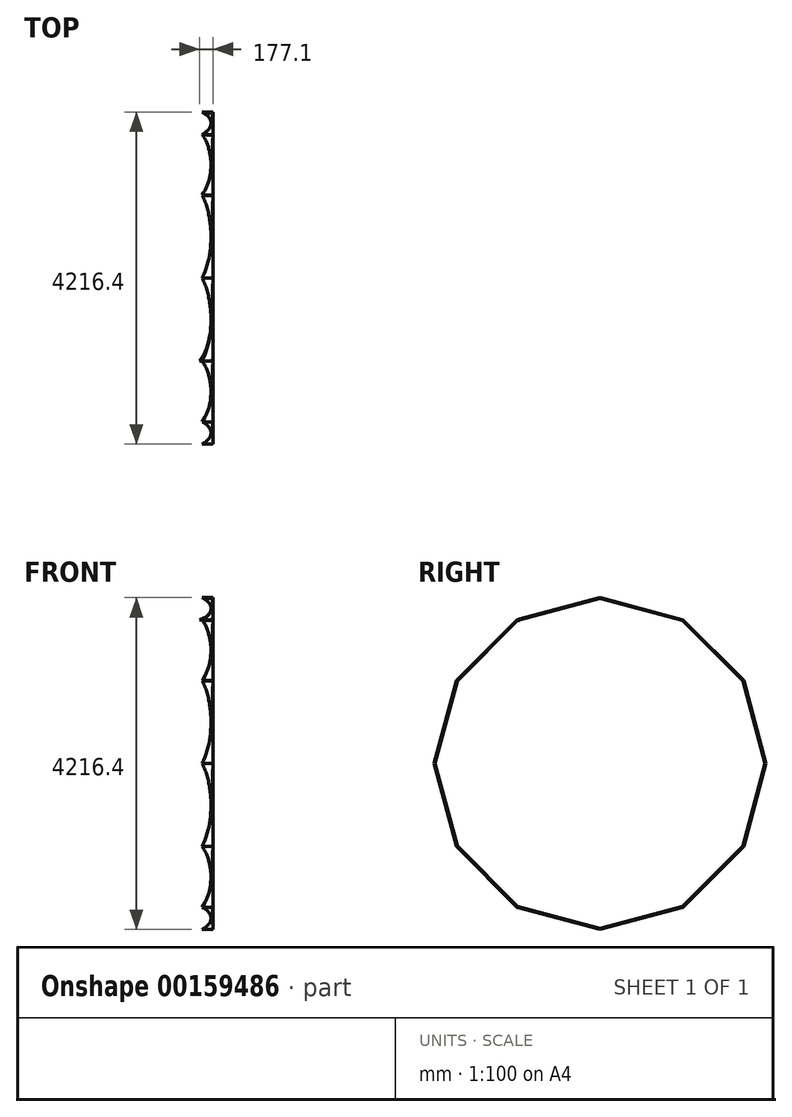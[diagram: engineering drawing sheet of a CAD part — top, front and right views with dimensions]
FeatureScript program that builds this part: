
annotation { "Feature Type Name" : "Feature", "Feature Type Description" : "" }
export const myFeature = defineFeature(function(context is Context, id is Id, definition is map)
    precondition{}
    {
        {
            var Q0;
            Q0=qCreatedBy(makeId("Top.planeOp"),FACE);
            var sketch = newSketch(context, id + "F0", { "sketchPlane" : qUnion([Q0])});
            skCircle(sketch, "E0", {"center": v(0, 0) * mm, "radius": 2159 * mm, "construction": true});
            skCircle(sketch, "E1.1.0.0", {"center": v(2159, 0) * mm, "radius": 2159 * mm, "construction": true});
            skCircle(sketch, "E1.2.0.0", {"center": v(4318, 0) * mm, "radius": 2159 * mm, "construction": true});
            skCircle(sketch, "E1.3.0.0", {"center": v(6477, 0) * mm, "radius": 2159 * mm, "construction": true});
            skLineSegment(sketch, "E1.direction1", {"start": v(0, 0) * mm, "end": v(2159, 0) * mm, "construction": true});
            skLineSegment(sketch, "E2", {"start": v(0, 0) * mm, "end": v(-6666.76, 0) * mm, "construction": true});
            skLineSegment(sketch, "E3", {"start": v(0, 0) * mm, "end": v(-3812.7, 2201.26) * mm, "construction": true});
            skLineSegment(sketch, "E4", {"start": v(0, 0) * mm, "end": v(0, 5036.56) * mm, "construction": true});
            skLineSegment(sketch, "E5", {"start": v(0, 0) * mm, "end": v(5007.78, 2891.24) * mm, "construction": true});
            skCircle(sketch, "E6.MirrorC", {"center": v(2159, 3739.5) * mm, "radius": 2159 * mm, "construction": true});
            skCircle(sketch, "E7.MirrorC", {"center": v(3238.5, 5609.25) * mm, "radius": 2159 * mm, "construction": true});
            skCircle(sketch, "E8.MirrorC", {"center": v(1079.5, 1869.75) * mm, "radius": 2159 * mm, "construction": true});
            skCircle(sketch, "E9.MirrorC", {"center": v(-3238.5, 5609.25) * mm, "radius": 2159 * mm, "construction": true});
            skCircle(sketch, "E10.MirrorC", {"center": v(-2159, 3739.5) * mm, "radius": 2159 * mm, "construction": true});
            skCircle(sketch, "E11.MirrorC", {"center": v(-1079.5, 1869.75) * mm, "radius": 2159 * mm, "construction": true});
            skCircle(sketch, "E12.MirrorC", {"center": v(-2159, 0) * mm, "radius": 2159 * mm, "construction": true});
            skCircle(sketch, "E13.MirrorC", {"center": v(-6477, 0) * mm, "radius": 2159 * mm, "construction": true});
            skCircle(sketch, "E14.MirrorC", {"center": v(-4318, 0) * mm, "radius": 2159 * mm, "construction": true});
            skCircle(sketch, "E15.MirrorC", {"center": v(-3238.5, -5609.25) * mm, "radius": 2159 * mm, "construction": true});
            skCircle(sketch, "E16.MirrorC", {"center": v(-2159, -3739.5) * mm, "radius": 2159 * mm, "construction": true});
            skCircle(sketch, "E17.MirrorC", {"center": v(-1079.5, -1869.75) * mm, "radius": 2159 * mm, "construction": true});
            skCircle(sketch, "E18.MirrorC", {"center": v(3238.5, -5609.25) * mm, "radius": 2159 * mm, "construction": true});
            skCircle(sketch, "E19.MirrorC", {"center": v(2159, -3739.5) * mm, "radius": 2159 * mm, "construction": true});
            skCircle(sketch, "E20.MirrorC", {"center": v(1079.5, -1869.75) * mm, "radius": 2159 * mm, "construction": true});
            skSolve(sketch);
        }
        {
            var Q0;
            Q0=qCreatedBy(makeId("Front.planeOp"),FACE);
            var sketch = newSketch(context, id + "F1", { "sketchPlane" : qUnion([Q0])});
            skCircle(sketch, "E21", {"center": v(0, 0) * mm, "radius": 2159 * mm, "construction": true});
            skPoint(sketch, "E22", {"position": v(2159, 0) * mm});
            skCircle(sketch, "E23", {"center": v(2159, 0) * mm, "radius": 2159 * mm, "construction": true});
            skPoint(sketch, "E24", {"position": v(4318, 0) * mm});
            skCircle(sketch, "E25", {"center": v(4318, 0) * mm, "radius": 2159 * mm, "construction": true});
            skPoint(sketch, "E26", {"position": v(6477, 0) * mm});
            skLineSegment(sketch, "E27", {"start": v(0, 0) * mm, "end": v(0, 2589.87) * mm, "construction": true});
            skLineSegment(sketch, "E28", {"start": v(0, 0) * mm, "end": v(2676.41, 1545.23) * mm, "construction": true});
            skCircle(sketch, "E29", {"center": v(6477, 0) * mm, "radius": 2159 * mm, "construction": true});
            skCircle(sketch, "E30.MirrorC", {"center": v(3238.5, 5609.25) * mm, "radius": 2159 * mm, "construction": true});
            skCircle(sketch, "E31.MirrorC", {"center": v(2159, 3739.5) * mm, "radius": 2159 * mm, "construction": true});
            skCircle(sketch, "E32.MirrorC", {"center": v(1079.5, 1869.75) * mm, "radius": 2159 * mm, "construction": true});
            skLineSegment(sketch, "E33.MirrorCS", {"start": v(0, 0) * mm, "end": v(2242.9, -1294.93) * mm, "construction": true});
            skCircle(sketch, "E34.MirrorC", {"center": v(-3238.5, 5609.25) * mm, "radius": 2159 * mm, "construction": true});
            skCircle(sketch, "E35.MirrorC", {"center": v(-2159, 3739.5) * mm, "radius": 2159 * mm, "construction": true});
            skCircle(sketch, "E36.MirrorC", {"center": v(-1079.5, 1869.75) * mm, "radius": 2159 * mm, "construction": true});
            skCircle(sketch, "E37.MirrorC", {"center": v(-6477, 0) * mm, "radius": 2159 * mm, "construction": true});
            skCircle(sketch, "E38.MirrorC", {"center": v(-4318, 0) * mm, "radius": 2159 * mm, "construction": true});
            skCircle(sketch, "E39.MirrorC", {"center": v(-2159, 0) * mm, "radius": 2159 * mm, "construction": true});
            skPoint(sketch, "E40", {"position": v(-8636, 0) * mm});
            skSolve(sketch);
        }
        {
            var Q0;
            Q0=qCreatedBy(makeId("Front.planeOp"),FACE);
            var sketch = newSketch(context, id + "F2", { "sketchPlane" : qUnion([Q0])});
            skLineSegment(sketch, "E41", {"start": v(-6477, 0) * mm, "end": v(-10795, 0) * mm, "construction": true});
            skLineSegment(sketch, "E42", {"start": v(-6477, 0) * mm, "end": v(-6287.7, 2150.68) * mm, "construction": true});
            skArc(sketch, "E43", {"start": v(-6287.7, 2150.68) * mm, "mid": v(-8535.9, 649.77) * mm, "end": v(-7556.5, -1869.75) * mm, "construction": true});
            skLineSegment(sketch, "E44", {"start": v(-10795, 0) * mm, "end": v(-6128.11, 2694.43) * mm, "construction": true});
            skLineSegment(sketch, "E45", {"start": v(-6128.11, 2694.43) * mm, "end": v(-6287.7, 2150.68) * mm, "construction": true});
            skLineSegment(sketch, "E46", {"start": v(-10795, 0) * mm, "end": v(-7556.5, -1869.75) * mm, "construction": true});
            skArc(sketch, "E47", {"start": v(-7094.56, -2136.45) * mm, "mid": v(-6603.97, -4563.1) * mm, "end": v(-9072.79, -4748.22) * mm, "construction": true});
            skLineSegment(sketch, "E48", {"start": v(-1291.7, -5064.86) * mm, "end": v(-1291.7, -5369.66) * mm, "construction": true});
            skLineSegment(sketch, "E49", {"start": v(-1291.7, -5369.66) * mm, "end": v(-10149.15, -5369.66) * mm, "construction": true});
            skLineSegment(sketch, "E50", {"start": v(-10149.15, -5369.66) * mm, "end": v(-9072.79, -4748.22) * mm, "construction": true});
            skLineSegment(sketch, "E51", {"start": v(-6128.11, 2694.43) * mm, "end": v(0, 6232.5) * mm, "construction": true});
            skLineSegment(sketch, "E52", {"start": v(0, -5369.66) * mm, "end": v(-1291.7, -5369.66) * mm, "construction": true});
            skLineSegment(sketch, "E53", {"start": v(-6571, -2016.86) * mm, "end": v(-1291.7, -5064.86) * mm, "construction": true});
            skLineSegment(sketch, "E54", {"start": v(-9847.47, 547.06) * mm, "end": v(-9847.47, -547.06) * mm, "construction": true});
            skPoint(sketch, "E55", {"position": v(-9847.47, 0) * mm});
            skLineSegment(sketch, "E56", {"start": v(-6269.06, -880.15) * mm, "end": v(-6269.06, -5369.66) * mm, "construction": true});
            skLineSegment(sketch, "E57", {"start": v(-7556.5, -1869.75) * mm, "end": v(-7116.56, -2123.75) * mm, "construction": true});
            skLineSegment(sketch, "E58", {"start": v(-7920.06, -5217.26) * mm, "end": v(-7920.06, -5369.66) * mm, "construction": true});
            skLineSegment(sketch, "E59", {"start": v(-7920.06, -3566.26) * mm, "end": v(-7920.06, -5217.26) * mm, "construction": true});
            skLineSegment(sketch, "E60", {"start": v(0, 0) * mm, "end": v(0, -5369.66) * mm, "construction": true});
            skPoint(sketch, "E61", {"position": v(-7094.56, -2136.45) * mm});
            skLineSegment(sketch, "E62", {"start": v(-7116.56, -2123.75) * mm, "end": v(-7094.56, -2136.45) * mm, "construction": true});
            skLineSegment(sketch, "E63", {"start": v(-6571, -2016.86) * mm, "end": v(-7247.43, -2016.86) * mm, "construction": true});
            skLineSegment(sketch, "E64", {"start": v(-7540.26, -2016.86) * mm, "end": v(-7540.26, -1533.1) * mm, "construction": true});
            skLineSegment(sketch, "E65", {"start": v(-7540.26, -1533.1) * mm, "end": v(-7997.16, -1533.1) * mm, "construction": true});
            skLineSegment(sketch, "E66", {"start": v(-7997.16, -1533.1) * mm, "end": v(-7997.16, -1407.26) * mm, "construction": true});
            skLineSegment(sketch, "E67", {"start": v(-7997.16, -1407.26) * mm, "end": v(-8114.35, -1407.26) * mm, "construction": true});
            skLineSegment(sketch, "E68", {"start": v(-6477, 0) * mm, "end": v(-6477, 2159) * mm, "construction": true});
            skLineSegment(sketch, "E69", {"start": v(-8114.35, 1407.26) * mm, "end": v(-7854.63, 1407.26) * mm, "construction": true});
            skLineSegment(sketch, "E70", {"start": v(-7854.63, 1407.26) * mm, "end": v(-7854.63, -1407.26) * mm, "construction": true});
            skPoint(sketch, "E71", {"position": v(-7854.63, 0) * mm});
            skSolve(sketch);
        }
        {
            var Q0;
            Q0=qCreatedBy(makeId("Front.planeOp"),FACE);
            var sketch = newSketch(context, id + "F3", { "sketchPlane" : qUnion([Q0])});
            skArc(sketch, "E72", {"start": v(-8636, 0) * mm, "mid": v(-7935.18, 1592.17) * mm, "end": v(-6287.7, 2150.68) * mm});
            skSolve(sketch);
        }
        {
            var Q0;
            Q0=sQuery(id+"F3.wireOp",VERTEX,"E72.start");
            var Q1;
            Q1=qCreatedBy(makeId("Top.planeOp"),FACE);
            cPlane(context, id + "F4", {"entities" : qUnion([Q0, Q1]), "cplaneType" : CPlaneType.PLANE_POINT, "offset" : 25.4 * mm, "width" : 152.4 * mm, "height" : 152.4 * mm});
        }
        {
            var Q0;
            Q0=qCreatedBy(id+"F4.planeOp",FACE);
            var sketch = newSketch(context, id + "F5", { "sketchPlane" : qUnion([Q0])});
            skLineSegment(sketch, "E73.bottom", {"start": v(-8591.55, 25.4) * mm, "end": v(-8629.65, 25.4) * mm});
            skLineSegment(sketch, "E73.top", {"start": v(-8591.55, -25.4) * mm, "end": v(-8629.65, -25.4) * mm});
            skLineSegment(sketch, "E73.left", {"start": v(-8585.2, 19.05) * mm, "end": v(-8585.2, -19.05) * mm});
            skLineSegment(sketch, "E73.right", {"start": v(-8636, 19.05) * mm, "end": v(-8636, -19.05) * mm});
            skPoint(sketch, "E74.visualSharp", {"position": v(-8585.2, 25.4) * mm});
            skArc(sketch, "E74.filletArc", {"start": v(-8585.2, 19.05) * mm, "mid": v(-8587.06, 23.54) * mm, "end": v(-8591.55, 25.4) * mm});
            skPoint(sketch, "E75.visualSharp", {"position": v(-8585.2, -25.4) * mm});
            skArc(sketch, "E75.filletArc", {"start": v(-8591.55, -25.4) * mm, "mid": v(-8587.06, -23.54) * mm, "end": v(-8585.2, -19.05) * mm});
            skPoint(sketch, "E76.visualSharp", {"position": v(-8636, -25.4) * mm});
            skArc(sketch, "E76.filletArc", {"start": v(-8636, -19.05) * mm, "mid": v(-8634.14, -23.54) * mm, "end": v(-8629.65, -25.4) * mm});
            skPoint(sketch, "E77.visualSharp", {"position": v(-8636, 25.4) * mm});
            skArc(sketch, "E77.filletArc", {"start": v(-8629.65, 25.4) * mm, "mid": v(-8634.14, 23.54) * mm, "end": v(-8636, 19.05) * mm});
            skLineSegment(sketch, "E78.0", {"start": v(-8589.96, 20.64) * mm, "end": v(-8589.96, -20.64) * mm});
            skLineSegment(sketch, "E78.1", {"start": v(-8589.96, 20.64) * mm, "end": v(-8631.24, 20.64) * mm});
            skLineSegment(sketch, "E78.2", {"start": v(-8631.24, 20.64) * mm, "end": v(-8631.24, -20.64) * mm});
            skLineSegment(sketch, "E78.3", {"start": v(-8589.96, -20.64) * mm, "end": v(-8631.24, -20.64) * mm});
            skSolve(sketch);
        }
        {
            var Q0;
            Q0=makeQuery(id+"F5.imprint","IMPRINT",FACE,{"disambiguationData":[TD([[makeQuery(id+"F5.imprint","IMPRINT",EDGE,{"derivedFrom":sQuery(id+"F5.wireOp",EDGE,"E73.bottom")}),1.0]])]});
            var Q1;
            Q1=sQuery(id+"F3.wireOp",EDGE,"E72");
            sweep(context, id + "F6", {"profiles" : qUnion([Q0]), "path" : qUnion([Q1])});
        }
        {
            var Q0;
            Q0=qCreatedBy(makeId("Front.planeOp"),FACE);
            var sketch = newSketch(context, id + "F7", { "sketchPlane" : qUnion([Q0])});
            skArc(sketch, "E79", {"start": v(-8636, 0) * mm, "mid": v(-8346.75, -1079.5) * mm, "end": v(-7556.5, -1869.75) * mm});
            skLineSegment(sketch, "E80", {"start": v(-7556.5, -1869.75) * mm, "end": v(-7116.56, -2123.75) * mm});
            skSolve(sketch);
        }
        {
            var Q0;
            Q0=qSketchRegion(id+"F5",true);
            var Q1;
            Q1=sQuery(id+"F7.wireOp",EDGE,"E79");
            var Q2;
            Q2=sQuery(id+"F7.wireOp",EDGE,"E80");
            sweep(context, id + "F8", {"profiles" : qUnion([Q0]), "path" : qUnion([Q1, Q2])});
        }
        {
            var Q0;
            Q0=qCreatedBy(makeId("Front.planeOp"),FACE);
            var sketch = newSketch(context, id + "F9", { "sketchPlane" : qUnion([Q0])});
            skArc(sketch, "E81", {"start": v(-7094.56, -2136.45) * mm, "mid": v(-6603.97, -4563.1) * mm, "end": v(-9072.79, -4748.22) * mm});
            skLineSegment(sketch, "E82", {"start": v(-7094.56, -2136.45) * mm, "end": v(-7116.56, -2123.75) * mm});
            skLineSegment(sketch, "E83", {"start": v(-7116.56, -2123.75) * mm, "end": v(-7556.5, -1869.75) * mm});
            skSolve(sketch);
        }
        {
            var Q0;
            Q0=makeQuery(id+"F8.opSweep","CAP_FACE",FACE,{"disambiguationData":[OSD([sQuery(id+"F5.wireOp",EDGE,"E73.bottom"),sQuery(id+"F5.wireOp",EDGE,"E73.top"),sQuery(id+"F5.wireOp",EDGE,"E73.left"),sQuery(id+"F5.wireOp",EDGE,"E73.right"),sQuery(id+"F5.wireOp",EDGE,"E74.filletArc"),sQuery(id+"F5.wireOp",EDGE,"E75.filletArc"),sQuery(id+"F5.wireOp",EDGE,"E76.filletArc"),sQuery(id+"F5.wireOp",EDGE,"E77.filletArc"),sQuery(id+"F5.wireOp",EDGE,"E78.0"),sQuery(id+"F5.wireOp",EDGE,"E78.1"),sQuery(id+"F5.wireOp",EDGE,"E78.2"),sQuery(id+"F5.wireOp",EDGE,"E78.3"),sQuery(id+"F7.wireOp",VERTEX,"E80.end")])],"isStart":false});
            var Q1;
            Q1=makeQuery(id+"F8.opSweep","CAP_VERTEX",VERTEX,{"disambiguationData":[OSD([sQuery(id+"F5.wireOp",EDGE,"E78.1"),sQuery(id+"F5.wireOp",EDGE,"E78.2"),sQuery(id+"F7.wireOp",EDGE,"E80")])],"isStart":false});
            cPlane(context, id + "F10", {"entities" : qUnion([Q0, Q1]), "cplaneType" : CPlaneType.PLANE_POINT, "offset" : 25.4 * mm, "width" : 152.4 * mm, "height" : 152.4 * mm});
        }
        {
            var Q0;
            Q0=qCreatedBy(id+"F10.planeOp",FACE);
            var sketch = newSketch(context, id + "F11", { "sketchPlane" : qUnion([Q0])});
            skLineSegment(sketch, "E84.bottom", {"start": v(19.05, -5397.5) * mm, "end": v(-19.05, -5397.5) * mm});
            skLineSegment(sketch, "E84.top", {"start": v(19.05, -5448.3) * mm, "end": v(-19.05, -5448.3) * mm});
            skLineSegment(sketch, "E84.left", {"start": v(25.4, -5403.85) * mm, "end": v(25.4, -5441.95) * mm});
            skLineSegment(sketch, "E84.right", {"start": v(-25.4, -5403.85) * mm, "end": v(-25.4, -5441.95) * mm});
            skPoint(sketch, "E85.visualSharp", {"position": v(25.4, -5397.5) * mm});
            skArc(sketch, "E85.filletArc", {"start": v(25.4, -5403.85) * mm, "mid": v(23.54, -5399.36) * mm, "end": v(19.05, -5397.5) * mm});
            skPoint(sketch, "E86.visualSharp", {"position": v(25.4, -5448.3) * mm});
            skArc(sketch, "E86.filletArc", {"start": v(19.05, -5448.3) * mm, "mid": v(23.54, -5446.44) * mm, "end": v(25.4, -5441.95) * mm});
            skPoint(sketch, "E87.visualSharp", {"position": v(-25.4, -5448.3) * mm});
            skArc(sketch, "E87.filletArc", {"start": v(-25.4, -5441.95) * mm, "mid": v(-23.54, -5446.44) * mm, "end": v(-19.05, -5448.3) * mm});
            skPoint(sketch, "E88.visualSharp", {"position": v(-25.4, -5397.5) * mm});
            skArc(sketch, "E88.filletArc", {"start": v(-19.05, -5397.5) * mm, "mid": v(-23.54, -5399.36) * mm, "end": v(-25.4, -5403.85) * mm});
            skLineSegment(sketch, "E89.0", {"start": v(20.64, -5402.26) * mm, "end": v(20.64, -5443.54) * mm});
            skLineSegment(sketch, "E89.1", {"start": v(20.64, -5402.26) * mm, "end": v(-20.64, -5402.26) * mm});
            skLineSegment(sketch, "E89.2", {"start": v(-20.64, -5402.26) * mm, "end": v(-20.64, -5443.54) * mm});
            skLineSegment(sketch, "E89.3", {"start": v(20.64, -5443.54) * mm, "end": v(-20.64, -5443.54) * mm});
            skSolve(sketch);
        }
        {
            var Q0;
            Q0=makeQuery(id+"F11.imprint","IMPRINT",FACE,{"disambiguationData":[TD([[makeQuery(id+"F11.imprint","IMPRINT",EDGE,{"derivedFrom":sQuery(id+"F11.wireOp",EDGE,"E84.bottom")}),1.0]])]});
            var Q1;
            Q1=sQuery(id+"F9.wireOp",EDGE,"E82");
            var Q2;
            Q2=sQuery(id+"F9.wireOp",EDGE,"E81");
            sweep(context, id + "F12", {"profiles" : qUnion([Q0]), "path" : qUnion([Q1, Q2])});
        }
        {
            var Q0;
            Q0=makeQuery(id+"F11.imprint","IMPRINT",FACE,{"disambiguationData":[TD([[makeQuery(id+"F11.imprint","IMPRINT",EDGE,{"derivedFrom":sQuery(id+"F11.wireOp",EDGE,"E84.bottom")}),1.0]])]});
            var Q1;
            Q1=sQuery(id+"F9.wireOp",EDGE,"E83");
            sweep(context, id + "F13", {"operationType" : NewBodyOperationType.ADD, "profiles" : qUnion([Q0]), "path" : qUnion([Q1])});
        }
        {
            var Q0;
            Q0=qCreatedBy(id+"F10.planeOp",FACE);
            var sketch = newSketch(context, id + "F14", { "sketchPlane" : qUnion([Q0])});
            skArc(sketch, "E90.0", {"start": v(-19.05, -5346.7) * mm, "mid": v(-23.54, -5348.56) * mm, "end": v(-25.4, -5353.05) * mm});
            skLineSegment(sketch, "E91.0", {"start": v(19.05, -5346.7) * mm, "end": v(-19.05, -5346.7) * mm});
            skArc(sketch, "E92.0", {"start": v(25.4, -5353.05) * mm, "mid": v(23.54, -5348.56) * mm, "end": v(19.05, -5346.7) * mm});
            skLineSegment(sketch, "E93.0", {"start": v(25.4, -5391.15) * mm, "end": v(25.4, -5353.05) * mm});
            skLineSegment(sketch, "E94.0", {"start": v(19.05, -5397.5) * mm, "end": v(-19.05, -5397.5) * mm});
            skLineSegment(sketch, "E95.0", {"start": v(-25.4, -5353.05) * mm, "end": v(-25.4, -5391.15) * mm});
            skArc(sketch, "E96.0", {"start": v(-19.05, -5397.5) * mm, "mid": v(-23.54, -5399.36) * mm, "end": v(-25.4, -5403.85) * mm});
            skLineSegment(sketch, "E97", {"start": v(-25.4, -5391.15) * mm, "end": v(-25.4, -5403.85) * mm});
            skArc(sketch, "E98.0", {"start": v(25.4, -5403.85) * mm, "mid": v(23.54, -5399.36) * mm, "end": v(19.05, -5397.5) * mm});
            skLineSegment(sketch, "E99", {"start": v(25.4, -5391.15) * mm, "end": v(25.4, -5403.85) * mm});
            skSolve(sketch);
        }
        {
            var Q0;
            Q0=qSketchRegion(id+"F14",true);
            extrude(context, id + "F15", {"entities" : qUnion([Q0]), "operationType" : NewBodyOperationType.ADD, "depth" : 6.35 * mm});
        }
        {
            var Q0;
            {var subQ0=sQuery(id+"F11.wireOp",EDGE,"E84.right");Q0=makeQuery(id+"F15.boolean.opBoolean","MERGE",FACE,{"derivedFrom":[makeQuery(id+"F13.boolean.opBoolean","MERGE",FACE,{"derivedFrom":[makeQuery(id+"F12.opSweep","SWEPT_FACE",FACE,{"disambiguationData":[OSD([sQuery(id+"F9.wireOp",EDGE,"E82"),subQ0])]}),makeQuery(id+"F13.opSweep","SWEPT_FACE",FACE,{"disambiguationData":[OSD([sQuery(id+"F9.wireOp",EDGE,"E83"),subQ0])]})]}),makeQuery(id+"F15.opExtrude","SWEPT_FACE",FACE,{"disambiguationData":[OSD([sQuery(id+"F14.wireOp",EDGE,"E95.0"),sQuery(id+"F14.wireOp",EDGE,"E97")])]})]});}
            var sketch = newSketch(context, id + "F16", { "sketchPlane" : qUnion([Q0])});
            skLineSegment(sketch, "E100", {"start": v(-7461.7, -1807.16) * mm, "end": v(-7329.72, -1883.36) * mm});
            skLineSegment(sketch, "E101", {"start": v(-7329.72, -1883.36) * mm, "end": v(-7431.32, -2059.34) * mm});
            skLineSegment(sketch, "E102", {"start": v(-7431.32, -2059.34) * mm, "end": v(-7563.3, -1983.14) * mm});
            skLineSegment(sketch, "E103", {"start": v(-7563.3, -1983.14) * mm, "end": v(-7461.7, -1807.16) * mm});
            skLineSegment(sketch, "E104", {"start": v(-7314.3, -1958.25) * mm, "end": v(-7358.75, -2035.24) * mm, "construction": true});
            skLineSegment(sketch, "E105.MirrorCS", {"start": v(-7343.34, -2110.14) * mm, "end": v(-7211.35, -2186.34) * mm});
            skLineSegment(sketch, "E106.MirrorCS", {"start": v(-7241.74, -1934.16) * mm, "end": v(-7343.34, -2110.14) * mm});
            skLineSegment(sketch, "E107.MirrorCS", {"start": v(-7109.75, -2010.36) * mm, "end": v(-7241.74, -1934.16) * mm});
            skLineSegment(sketch, "E108.MirrorCS", {"start": v(-7211.35, -2186.34) * mm, "end": v(-7109.75, -2010.36) * mm});
            skSolve(sketch);
        }
        {
            var Q0;
            Q0=sQuery(id+"F2.wireOp",VERTEX,"E56.end");
            var Q1;
            Q1=qCreatedBy(makeId("Top.planeOp"),FACE);
            cPlane(context, id + "F17", {"entities" : qUnion([Q0, Q1]), "cplaneType" : CPlaneType.PLANE_POINT, "offset" : 25.4 * mm, "width" : 152.4 * mm, "height" : 152.4 * mm});
        }
        {
            var Q0;
            Q0=qCreatedBy(id+"F17.planeOp",FACE);
            var sketch = newSketch(context, id + "F18", { "sketchPlane" : qUnion([Q0])});
            skLineSegment(sketch, "E109.bottom", {"start": v(-6224.61, 25.4) * mm, "end": v(-6262.71, 25.4) * mm});
            skLineSegment(sketch, "E109.top", {"start": v(-6224.61, -25.4) * mm, "end": v(-6262.71, -25.4) * mm});
            skLineSegment(sketch, "E109.left", {"start": v(-6218.26, 19.05) * mm, "end": v(-6218.26, -19.05) * mm});
            skLineSegment(sketch, "E109.right", {"start": v(-6269.06, 19.05) * mm, "end": v(-6269.06, -19.05) * mm});
            skPoint(sketch, "E110.visualSharp", {"position": v(-6218.26, 25.4) * mm});
            skArc(sketch, "E110.filletArc", {"start": v(-6218.26, 19.05) * mm, "mid": v(-6220.12, 23.54) * mm, "end": v(-6224.61, 25.4) * mm});
            skPoint(sketch, "E111.visualSharp", {"position": v(-6218.26, -25.4) * mm});
            skArc(sketch, "E111.filletArc", {"start": v(-6224.61, -25.4) * mm, "mid": v(-6220.12, -23.54) * mm, "end": v(-6218.26, -19.05) * mm});
            skPoint(sketch, "E112.visualSharp", {"position": v(-6269.06, -25.4) * mm});
            skArc(sketch, "E112.filletArc", {"start": v(-6269.06, -19.05) * mm, "mid": v(-6267.2, -23.54) * mm, "end": v(-6262.71, -25.4) * mm});
            skPoint(sketch, "E113.visualSharp", {"position": v(-6269.06, 25.4) * mm});
            skArc(sketch, "E113.filletArc", {"start": v(-6262.71, 25.4) * mm, "mid": v(-6267.2, 23.54) * mm, "end": v(-6269.06, 19.05) * mm});
            skLineSegment(sketch, "E114.0", {"start": v(-6223.02, 20.64) * mm, "end": v(-6223.02, -20.64) * mm});
            skLineSegment(sketch, "E114.1", {"start": v(-6223.02, 20.64) * mm, "end": v(-6264.3, 20.64) * mm});
            skLineSegment(sketch, "E114.2", {"start": v(-6264.3, 20.64) * mm, "end": v(-6264.3, -20.64) * mm});
            skLineSegment(sketch, "E114.3", {"start": v(-6223.02, -20.64) * mm, "end": v(-6264.3, -20.64) * mm});
            skSolve(sketch);
        }
        {
            var Q0;
            Q0=qSketchRegion(id+"F16",true);
            extrude(context, id + "F19", {"entities" : qUnion([Q0]), "operationType" : NewBodyOperationType.ADD, "depth" : 6.35 * mm});
        }
        {
            var Q0;
            {var subQ0=sQuery(id+"F11.wireOp",EDGE,"E84.left");Q0=makeQuery(id+"F15.boolean.opBoolean","MERGE",FACE,{"derivedFrom":[makeQuery(id+"F13.boolean.opBoolean","MERGE",FACE,{"derivedFrom":[makeQuery(id+"F12.opSweep","SWEPT_FACE",FACE,{"disambiguationData":[OSD([sQuery(id+"F9.wireOp",EDGE,"E82"),subQ0])]}),makeQuery(id+"F13.opSweep","SWEPT_FACE",FACE,{"disambiguationData":[OSD([sQuery(id+"F9.wireOp",EDGE,"E83"),subQ0])]})]}),makeQuery(id+"F15.opExtrude","SWEPT_FACE",FACE,{"disambiguationData":[OSD([sQuery(id+"F14.wireOp",EDGE,"E93.0"),sQuery(id+"F14.wireOp",EDGE,"E99")])]})]});}
            var sketch = newSketch(context, id + "F20", { "sketchPlane" : qUnion([Q0])});
            skLineSegment(sketch, "E115.0.0", {"start": v(7329.72, -1883.36) * mm, "end": v(7461.7, -1807.16) * mm});
            skLineSegment(sketch, "E115.0.1", {"start": v(7461.7, -1807.16) * mm, "end": v(7563.3, -1983.14) * mm});
            skLineSegment(sketch, "E115.0.2", {"start": v(7563.3, -1983.14) * mm, "end": v(7431.32, -2059.34) * mm});
            skLineSegment(sketch, "E115.0.3", {"start": v(7431.32, -2059.34) * mm, "end": v(7329.72, -1883.36) * mm});
            skLineSegment(sketch, "E116.0.0", {"start": v(7241.74, -1934.16) * mm, "end": v(7343.34, -2110.14) * mm});
            skLineSegment(sketch, "E116.0.1", {"start": v(7343.34, -2110.14) * mm, "end": v(7211.35, -2186.34) * mm});
            skLineSegment(sketch, "E116.0.2", {"start": v(7211.35, -2186.34) * mm, "end": v(7109.75, -2010.36) * mm});
            skLineSegment(sketch, "E116.0.3", {"start": v(7109.75, -2010.36) * mm, "end": v(7241.74, -1934.16) * mm});
            skSolve(sketch);
        }
        {
            var Q0;
            Q0=makeQuery(id+"F18.imprint","IMPRINT",FACE,{"disambiguationData":[TD([[makeQuery(id+"F18.imprint","IMPRINT",EDGE,{"derivedFrom":sQuery(id+"F18.wireOp",EDGE,"E109.bottom")}),1.0]])]});
            extrude(context, id + "F21", {"entities" : qUnion([Q0]), "operationType" : NewBodyOperationType.ADD, "depth" : 2870.2 * mm});
        }
        {
            var Q0;
            {var subQ1=sQuery(id+"F9.wireOp",EDGE,"E83");var subQ7=sQuery(id+"F14.wireOp",EDGE,"E97");var subQ9=sQuery(id+"F14.wireOp",EDGE,"E95.0");var subQ14=sQuery(id+"F14.wireOp",EDGE,"E90.0");var subQ15=sQuery(id+"F11.wireOp",EDGE,"E84.right");var subQ16=sQuery(id+"F9.wireOp",EDGE,"E82");Q0=makeQuery(id+"F19.boolean.opBoolean","SPLIT",FACE,{"disambiguationData":[TD([makeQuery(id+"F15.opExtrude","SWEPT_FACE",FACE,{"disambiguationData":[OSD([subQ14])]})])],"derivedFrom":makeQuery(id+"F15.boolean.opBoolean","MERGE",FACE,{"derivedFrom":[makeQuery(id+"F13.boolean.opBoolean","MERGE",FACE,{"derivedFrom":[makeQuery(id+"F12.opSweep","SWEPT_FACE",FACE,{"disambiguationData":[OSD([subQ16,subQ15])]}),makeQuery(id+"F13.opSweep","SWEPT_FACE",FACE,{"disambiguationData":[OSD([subQ1,subQ15])]})]}),makeQuery(id+"F15.opExtrude","SWEPT_FACE",FACE,{"disambiguationData":[OSD([subQ9,subQ7])]})]})});}
            var sketch = newSketch(context, id + "F22", { "sketchPlane" : qUnion([Q0])});
            skLineSegment(sketch, "E117", {"start": v(-7167.36, -2211.74) * mm, "end": v(-7065.76, -2035.76) * mm});
            skLineSegment(sketch, "E118", {"start": v(-7065.76, -2035.76) * mm, "end": v(-6218.26, -2525.06) * mm});
            skLineSegment(sketch, "E119", {"start": v(-6218.26, -2525.06) * mm, "end": v(-6218.26, -2759.7) * mm});
            skLineSegment(sketch, "E120", {"start": v(-6218.26, -2759.7) * mm, "end": v(-7167.36, -2211.74) * mm});
            skSolve(sketch);
        }
        {
            var Q0;
            Q0=qSketchRegion(id+"F22",true);
            extrude(context, id + "F23", {"entities" : qUnion([Q0]), "operationType" : NewBodyOperationType.ADD, "depth" : 6.35 * mm});
        }
        {
            var Q0;
            {var subQ1=sQuery(id+"F11.wireOp",EDGE,"E84.left");Q0=makeQuery(id+"F20.imprint","IMPRINT",FACE,{"disambiguationData":[TD([[makeQuery(id+"F20.imprint","IMPRINT",EDGE,{"derivedFrom":makeQuery(id+"F12.opSweep","CAP_EDGE",EDGE,{"disambiguationData":[OSD([sQuery(id+"F9.wireOp",VERTEX,"E81.end"),subQ1])],"isStart":false})}),-1.0]])]});}
            var sketch = newSketch(context, id + "F24", { "sketchPlane" : qUnion([Q0])});
            skLineSegment(sketch, "E121.0.0", {"start": v(7065.76, -2035.76) * mm, "end": v(7167.36, -2211.74) * mm});
            skLineSegment(sketch, "E121.0.1", {"start": v(7167.36, -2211.74) * mm, "end": v(6218.26, -2759.7) * mm});
            skLineSegment(sketch, "E121.0.2", {"start": v(6218.26, -2759.7) * mm, "end": v(6218.26, -2525.06) * mm});
            skLineSegment(sketch, "E121.0.3", {"start": v(6218.26, -2525.06) * mm, "end": v(7065.76, -2035.76) * mm});
            skSolve(sketch);
        }
        {
            var Q0;
            Q0=qSketchRegion(id+"F24",true);
            extrude(context, id + "F25", {"entities" : qUnion([Q0]), "operationType" : NewBodyOperationType.ADD, "depth" : 6.35 * mm});
        }
        {
            var Q0;
            Q0=qSketchRegion(id+"F20",true);
            extrude(context, id + "F26", {"entities" : qUnion([Q0]), "operationType" : NewBodyOperationType.ADD, "depth" : 6.35 * mm});
        }
        {
            var Q0;
            {var subQ0=sQuery(id+"F11.wireOp",EDGE,"E84.top");Q0=makeQuery(id+"F13.boolean.opBoolean","MERGE",FACE,{"derivedFrom":[makeQuery(id+"F12.opSweep","SWEPT_FACE",FACE,{"disambiguationData":[OSD([sQuery(id+"F9.wireOp",EDGE,"E82"),subQ0])]}),makeQuery(id+"F13.opSweep","SWEPT_FACE",FACE,{"disambiguationData":[OSD([sQuery(id+"F9.wireOp",EDGE,"E83"),subQ0])]})]});}
            var sketch = newSketch(context, id + "F27", { "sketchPlane" : qUnion([Q0])});
            skLineSegment(sketch, "E122", {"start": v(-5596.55, 0) * mm, "end": v(-5596.55, 57.15) * mm});
            skLineSegment(sketch, "E123", {"start": v(-5596.55, 57.15) * mm, "end": v(-5558.45, 57.15) * mm});
            skLineSegment(sketch, "E124", {"start": v(-5558.45, 57.15) * mm, "end": v(-5558.45, -57.15) * mm});
            skLineSegment(sketch, "E125", {"start": v(-5558.45, -57.15) * mm, "end": v(-5596.55, -57.15) * mm});
            skLineSegment(sketch, "E126", {"start": v(-5596.55, -57.15) * mm, "end": v(-5596.55, 0) * mm});
            skLineSegment(sketch, "E127.1.0.0", {"start": v(-5336.2, 57.15) * mm, "end": v(-5336.2, -57.15) * mm});
            skLineSegment(sketch, "E127.1.0.1", {"start": v(-5374.3, 57.15) * mm, "end": v(-5336.2, 57.15) * mm});
            skLineSegment(sketch, "E127.1.0.2", {"start": v(-5374.3, 0) * mm, "end": v(-5374.3, 57.15) * mm});
            skLineSegment(sketch, "E127.1.0.3", {"start": v(-5374.3, -57.15) * mm, "end": v(-5374.3, 0) * mm});
            skLineSegment(sketch, "E127.1.0.4", {"start": v(-5336.2, -57.15) * mm, "end": v(-5374.3, -57.15) * mm});
            skLineSegment(sketch, "E127.2.0.0", {"start": v(-5113.95, 57.15) * mm, "end": v(-5113.95, -57.15) * mm});
            skLineSegment(sketch, "E127.2.0.1", {"start": v(-5152.05, 57.15) * mm, "end": v(-5113.95, 57.15) * mm});
            skLineSegment(sketch, "E127.2.0.2", {"start": v(-5152.05, 0) * mm, "end": v(-5152.05, 57.15) * mm});
            skLineSegment(sketch, "E127.2.0.3", {"start": v(-5152.05, -57.15) * mm, "end": v(-5152.05, 0) * mm});
            skLineSegment(sketch, "E127.2.0.4", {"start": v(-5113.95, -57.15) * mm, "end": v(-5152.05, -57.15) * mm});
            skLineSegment(sketch, "E127.direction1", {"start": v(-5596.55, -57.15) * mm, "end": v(-5374.3, -57.15) * mm, "construction": true});
            skLineSegment(sketch, "E128", {"start": v(-5596.55, 0) * mm, "end": v(-5609.25, 0) * mm, "construction": true});
            skSolve(sketch);
        }
        {
            var Q0;
            Q0=qSketchRegion(id+"F27",true);
            extrude(context, id + "F28", {"entities" : qUnion([Q0]), "operationType" : NewBodyOperationType.ADD, "depth" : 6.35 * mm});
        }
        {
            var Q0;
            Q0=makeQuery(id+"F19.opExtrude","CAP_FACE",FACE,{"disambiguationData":[OSD([sQuery(id+"F16.wireOp",EDGE,"E100"),sQuery(id+"F16.wireOp",EDGE,"E101"),sQuery(id+"F16.wireOp",EDGE,"E102"),sQuery(id+"F16.wireOp",EDGE,"E103")])],"isStart":false});
            cPlane(context, id + "F29", {"entities" : qUnion([Q0]), "cplaneType" : CPlaneType.OFFSET, "offset" : 38.1 * mm, "width" : 152.4 * mm, "height" : 152.4 * mm});
        }
        {
            var Q0;
            Q0=qCreatedBy(id+"F29.planeOp",FACE);
            var sketch = newSketch(context, id + "F30", { "sketchPlane" : qUnion([Q0])});
            skLineSegment(sketch, "E129", {"start": v(-7480.3, -1737.77) * mm, "end": v(-1795.64, -5019.8) * mm});
            skLineSegment(sketch, "E130", {"start": v(-1795.64, -5019.8) * mm, "end": v(-1795.64, -5369.66) * mm});
            skLineSegment(sketch, "E131.0", {"start": v(-7626.35, -1990.73) * mm, "end": v(-1773.88, -5369.66) * mm});
            skLineSegment(sketch, "E132", {"start": v(-7480.3, -1737.77) * mm, "end": v(-7626.35, -1990.73) * mm});
            skLineSegment(sketch, "E133", {"start": v(-1795.64, -5369.66) * mm, "end": v(-1773.88, -5369.66) * mm});
            skSolve(sketch);
        }
        {
            var Q0;
            Q0=qCreatedBy(id+"F29.planeOp",FACE);
            var sketch = newSketch(context, id + "F31", { "sketchPlane" : qUnion([Q0])});
            skLineSegment(sketch, "E134.1", {"start": v(-7439.38, -2098.68) * mm, "end": v(-7293.33, -1845.72) * mm});
            skLineSegment(sketch, "E134.3", {"start": v(-7593.35, -2009.78) * mm, "end": v(-7439.38, -2098.68) * mm});
            skLineSegment(sketch, "E134.4", {"start": v(-7447.3, -1756.82) * mm, "end": v(-7593.35, -2009.78) * mm});
            skLineSegment(sketch, "E135", {"start": v(-7447.3, -1756.82) * mm, "end": v(-7293.33, -1845.72) * mm});
            skLineSegment(sketch, "E136", {"start": v(-7227.33, -1883.82) * mm, "end": v(-7373.38, -2136.78) * mm});
            skLineSegment(sketch, "E137", {"start": v(-7373.38, -2136.78) * mm, "end": v(-7219.4, -2225.68) * mm});
            skLineSegment(sketch, "E138", {"start": v(-7219.4, -2225.68) * mm, "end": v(-7073.35, -1972.72) * mm});
            skLineSegment(sketch, "E139", {"start": v(-7073.35, -1972.72) * mm, "end": v(-7227.33, -1883.82) * mm});
            skLineSegment(sketch, "E140.0", {"start": v(-7051.36, -1985.42) * mm, "end": v(-7197.4, -2238.38) * mm});
            skLineSegment(sketch, "E140.1", {"start": v(-6218.26, -2466.4) * mm, "end": v(-7051.36, -1985.42) * mm});
            skLineSegment(sketch, "E140.2", {"start": v(-6218.26, -2803.7) * mm, "end": v(-6218.26, -2466.4) * mm});
            skLineSegment(sketch, "E140.3", {"start": v(-7197.4, -2238.38) * mm, "end": v(-6218.26, -2803.7) * mm});
            skSolve(sketch);
        }
        {
            var Q0;
            Q0=makeQuery(id+"F30.imprint","IMPRINT",FACE,{"disambiguationData":[TD([[makeQuery(id+"F30.imprint","IMPRINT",EDGE,{"derivedFrom":sQuery(id+"F30.wireOp",EDGE,"E129")}),-1.0]])]});
            extrude(context, id + "F32", {"entities" : qUnion([Q0]), "depth" : 38.1 * mm});
        }
        {
            var Q0;
            Q0=makeQuery(id+"F26.opExtrude","CAP_FACE",FACE,{"disambiguationData":[OSD([sQuery(id+"F20.wireOp",EDGE,"E115.0.0"),sQuery(id+"F20.wireOp",EDGE,"E115.0.1"),sQuery(id+"F20.wireOp",EDGE,"E115.0.2"),sQuery(id+"F20.wireOp",EDGE,"E115.0.3")])],"isStart":false});
            cPlane(context, id + "F33", {"entities" : qUnion([Q0]), "cplaneType" : CPlaneType.OFFSET, "offset" : 38.1 * mm, "width" : 152.4 * mm, "height" : 152.4 * mm});
        }
        {
            var Q0;
            Q0=qCreatedBy(id+"F33.planeOp",FACE);
            var sketch = newSketch(context, id + "F34", { "sketchPlane" : qUnion([Q0])});
            skLineSegment(sketch, "E141.0.0", {"start": v(1795.64, -5019.8) * mm, "end": v(7480.3, -1737.77) * mm});
            skLineSegment(sketch, "E141.0.1", {"start": v(7480.3, -1737.77) * mm, "end": v(7626.35, -1990.73) * mm});
            skLineSegment(sketch, "E141.0.2", {"start": v(7626.35, -1990.73) * mm, "end": v(1795.64, -5357.1) * mm});
            skLineSegment(sketch, "E142.0", {"start": v(1795.64, -5019.8) * mm, "end": v(1795.64, -5019.8) * mm});
            skLineSegment(sketch, "E143", {"start": v(1795.64, -5019.8) * mm, "end": v(1795.64, -5357.1) * mm});
            skSolve(sketch);
        }
        {
            var Q0;
            Q0=qSketchRegion(id+"F34",true);
            extrude(context, id + "F35", {"entities" : qUnion([Q0]), "depth" : 38.1 * mm});
        }
        {
            var Q0;
            Q0=qSketchRegion(id+"F31",true);
            var Q1;
            Q1=makeQuery(id+"F19.opExtrude","CAP_FACE",FACE,{"disambiguationData":[OSD([sQuery(id+"F16.wireOp",EDGE,"E100"),sQuery(id+"F16.wireOp",EDGE,"E101"),sQuery(id+"F16.wireOp",EDGE,"E102"),sQuery(id+"F16.wireOp",EDGE,"E103")])],"isStart":false});
            extrude(context, id + "F36", {"entities" : qUnion([Q0]), "operationType" : NewBodyOperationType.ADD, "endBound" : BoundingType.UP_TO_SURFACE, "oppositeDirection" : true, "endBoundEntityFace" : qUnion([Q1]), "depth" : 25.4 * mm});
        }
        {
            var Q0;
            Q0=qCreatedBy(id+"F33.planeOp",FACE);
            var sketch = newSketch(context, id + "F37", { "sketchPlane" : qUnion([Q0])});
            skLineSegment(sketch, "E144.0.0", {"start": v(7439.38, -2098.68) * mm, "end": v(7593.35, -2009.78) * mm});
            skLineSegment(sketch, "E144.0.1", {"start": v(7593.35, -2009.78) * mm, "end": v(7447.3, -1756.82) * mm});
            skLineSegment(sketch, "E144.0.2", {"start": v(7447.3, -1756.82) * mm, "end": v(7293.33, -1845.72) * mm});
            skLineSegment(sketch, "E144.0.3", {"start": v(7293.33, -1845.72) * mm, "end": v(7439.38, -2098.68) * mm});
            skLineSegment(sketch, "E145.0.0", {"start": v(7227.33, -1883.82) * mm, "end": v(7073.35, -1972.72) * mm});
            skLineSegment(sketch, "E145.0.1", {"start": v(7073.35, -1972.72) * mm, "end": v(7219.4, -2225.68) * mm});
            skLineSegment(sketch, "E145.0.2", {"start": v(7219.4, -2225.68) * mm, "end": v(7373.38, -2136.78) * mm});
            skLineSegment(sketch, "E145.0.3", {"start": v(7373.38, -2136.78) * mm, "end": v(7227.33, -1883.82) * mm});
            skLineSegment(sketch, "E146.0.0", {"start": v(7051.36, -1985.42) * mm, "end": v(6218.26, -2466.4) * mm});
            skLineSegment(sketch, "E146.0.1", {"start": v(6218.26, -2466.4) * mm, "end": v(6218.26, -2803.7) * mm});
            skLineSegment(sketch, "E146.0.2", {"start": v(6218.26, -2803.7) * mm, "end": v(7197.4, -2238.38) * mm});
            skLineSegment(sketch, "E146.0.3", {"start": v(7197.4, -2238.38) * mm, "end": v(7051.36, -1985.42) * mm});
            skSolve(sketch);
        }
        {
            var Q0;
            Q0=qSketchRegion(id+"F37",true);
            var Q1;
            Q1=makeQuery(id+"F26.opExtrude","CAP_FACE",FACE,{"disambiguationData":[OSD([sQuery(id+"F20.wireOp",EDGE,"E116.0.0"),sQuery(id+"F20.wireOp",EDGE,"E116.0.1"),sQuery(id+"F20.wireOp",EDGE,"E116.0.2"),sQuery(id+"F20.wireOp",EDGE,"E116.0.3")])],"isStart":false});
            extrude(context, id + "F38", {"entities" : qUnion([Q0]), "operationType" : NewBodyOperationType.ADD, "endBound" : BoundingType.UP_TO_SURFACE, "oppositeDirection" : true, "endBoundEntityFace" : qUnion([Q1]), "depth" : 25.4 * mm});
        }
        {
            var Q0;
            Q0=sQuery(id+"F2.wireOp",EDGE,"E42");
            cPlane(context, id + "F39", {"entities" : qUnion([Q0]), "cplaneType" : CPlaneType.LINE_ANGLE, "offset" : 25.4 * mm, "angle" : 0 * degree, "width" : 152.4 * mm, "height" : 152.4 * mm});
        }
        {
            var Q0;
            Q0=qCreatedBy(makeId("Top.planeOp"),FACE);
            var sketch = newSketch(context, id + "F40", { "sketchPlane" : qUnion([Q0])});
            skArc(sketch, "E147", {"start": v(-8636, 0) * mm, "mid": v(-8003.64, -1526.64) * mm, "end": v(-6477, -2159) * mm});
            skSolve(sketch);
        }
        {
            var Q0;
            Q0=sQuery(id+"F40.wireOp",VERTEX,"E147.end");
            var Q1;
            Q1=sQuery(id+"F2.wireOp",EDGE,"E41");
            cPlane(context, id + "F41", {"entities" : qUnion([Q0, Q1]), "cplaneType" : CPlaneType.LINE_POINT, "offset" : 25.4 * mm, "width" : 152.4 * mm, "height" : 152.4 * mm});
        }
        {
            var Q0;
            Q0=qCreatedBy(id+"F41.planeOp",FACE);
            var sketch = newSketch(context, id + "F42", { "sketchPlane" : qUnion([Q0])});
            skLineSegment(sketch, "E148.bottom", {"start": v(2152.65, 25.4) * mm, "end": v(2114.55, 25.4) * mm});
            skLineSegment(sketch, "E148.top", {"start": v(2152.65, -25.4) * mm, "end": v(2114.55, -25.4) * mm});
            skLineSegment(sketch, "E148.left", {"start": v(2159, 19.05) * mm, "end": v(2159, -19.05) * mm});
            skLineSegment(sketch, "E148.right", {"start": v(2108.2, 19.05) * mm, "end": v(2108.2, -19.05) * mm});
            skPoint(sketch, "E149.visualSharp", {"position": v(2159, 25.4) * mm});
            skArc(sketch, "E149.filletArc", {"start": v(2159, 19.05) * mm, "mid": v(2157.14, 23.54) * mm, "end": v(2152.65, 25.4) * mm});
            skPoint(sketch, "E150.visualSharp", {"position": v(2159, -25.4) * mm});
            skArc(sketch, "E150.filletArc", {"start": v(2152.65, -25.4) * mm, "mid": v(2157.14, -23.54) * mm, "end": v(2159, -19.05) * mm});
            skPoint(sketch, "E151.visualSharp", {"position": v(2108.2, -25.4) * mm});
            skArc(sketch, "E151.filletArc", {"start": v(2108.2, -19.05) * mm, "mid": v(2110.06, -23.54) * mm, "end": v(2114.55, -25.4) * mm});
            skPoint(sketch, "E152.visualSharp", {"position": v(2108.2, 25.4) * mm});
            skArc(sketch, "E152.filletArc", {"start": v(2114.55, 25.4) * mm, "mid": v(2110.06, 23.54) * mm, "end": v(2108.2, 19.05) * mm});
            skLineSegment(sketch, "E153.0", {"start": v(2154.24, 20.64) * mm, "end": v(2154.24, -20.64) * mm});
            skLineSegment(sketch, "E153.1", {"start": v(2154.24, 20.64) * mm, "end": v(2112.96, 20.64) * mm});
            skLineSegment(sketch, "E153.2", {"start": v(2112.96, 20.64) * mm, "end": v(2112.96, -20.64) * mm});
            skLineSegment(sketch, "E153.3", {"start": v(2154.24, -20.64) * mm, "end": v(2112.96, -20.64) * mm});
            skSolve(sketch);
        }
        {
            var Q0;
            Q0=makeQuery(id+"F42.imprint","IMPRINT",FACE,{"disambiguationData":[TD([[makeQuery(id+"F42.imprint","IMPRINT",EDGE,{"derivedFrom":sQuery(id+"F42.wireOp",EDGE,"E148.bottom")}),1.0]])]});
            var Q1;
            Q1=sQuery(id+"F40.wireOp",EDGE,"E147");
            sweep(context, id + "F43", {"operationType" : NewBodyOperationType.ADD, "profiles" : qUnion([Q0]), "path" : qUnion([Q1])});
        }
        {
            var Q0;
            Q0=sQuery(id+"F2.wireOp",EDGE,"E68");
            cPlane(context, id + "F44", {"entities" : qUnion([Q0]), "cplaneType" : CPlaneType.LINE_ANGLE, "offset" : 25.4 * mm, "angle" : 0 * degree, "width" : 152.4 * mm, "height" : 152.4 * mm});
        }
        {
            var Q0;
            Q0=qCreatedBy(id+"F44.planeOp",FACE);
            var sketch = newSketch(context, id + "F45", { "sketchPlane" : qUnion([Q0])});
            skLineSegment(sketch, "E154", {"start": v(0, 2108.2) * mm, "end": v(-1054.1, 1825.75) * mm, "construction": true});
            skLineSegment(sketch, "E155", {"start": v(0, 2108.2) * mm, "end": v(0, 2061.86) * mm, "construction": true});
            skLineSegment(sketch, "E156", {"start": v(-19.05, 2108.2) * mm, "end": v(19.05, 2108.2) * mm});
            skArc(sketch, "E157", {"start": v(-25.4, 2114.55) * mm, "mid": v(-23.54, 2110.06) * mm, "end": v(-19.05, 2108.2) * mm});
            skLineSegment(sketch, "E158", {"start": v(-25.4, 2152.65) * mm, "end": v(-25.4, 2114.55) * mm});
            skLineSegment(sketch, "E159", {"start": v(-25.4, 2114.55) * mm, "end": v(-25.4, 2108.2) * mm});
            skLineSegment(sketch, "E160", {"start": v(-25.4, 2108.2) * mm, "end": v(-19.05, 2108.2) * mm});
            skLineSegment(sketch, "E161", {"start": v(0, 0) * mm, "end": v(-1054.1, 1825.75) * mm, "construction": true});
            skSolve(sketch);
        }
        {
            var Q0;
            Q0=sQuery(id+"F45.wireOp",VERTEX,"E154.end");
            var Q1;
            Q1=sQuery(id+"F45.wireOp",VERTEX,"E161.start");
            var Q2;
            Q2=sQuery(id+"F2.wireOp",VERTEX,"E55");
            cPlane(context, id + "F46", {"entities" : qUnion([Q0, Q1, Q2]), "cplaneType" : CPlaneType.THREE_POINT, "offset" : 25.4 * mm, "width" : 152.4 * mm, "height" : 152.4 * mm});
        }
        {
            var Q0;
            Q0=qCreatedBy(id+"F46.planeOp",FACE);
            var sketch = newSketch(context, id + "F47", { "sketchPlane" : qUnion([Q0])});
            skArc(sketch, "E162", {"start": v(-6477, 2159) * mm, "mid": v(-8003.64, 1526.64) * mm, "end": v(-8636, 0) * mm});
            skLineSegment(sketch, "E163", {"start": v(-7179.94, 2170.25) * mm, "end": v(-7179.94, 2060.02) * mm, "construction": true});
            skSolve(sketch);
        }
        {
            var Q0;
            Q0=qCreatedBy(id+"F44.planeOp",FACE);
            var sketch = newSketch(context, id + "F48", { "sketchPlane" : qUnion([Q0])});
            skLineSegment(sketch, "E164.bottom", {"start": v(-1063, 1879.27) * mm, "end": v(-1096, 1860.22) * mm});
            skLineSegment(sketch, "E164.top", {"start": v(-1037.6, 1835.28) * mm, "end": v(-1070.6, 1816.23) * mm});
            skLineSegment(sketch, "E164.left", {"start": v(-1054.33, 1876.95) * mm, "end": v(-1035.28, 1843.95) * mm});
            skLineSegment(sketch, "E164.right", {"start": v(-1098.32, 1851.55) * mm, "end": v(-1079.27, 1818.55) * mm});
            skPoint(sketch, "E165.visualSharp", {"position": v(-1057.5, 1882.45) * mm});
            skArc(sketch, "E165.filletArc", {"start": v(-1054.33, 1876.95) * mm, "mid": v(-1058.18, 1879.9) * mm, "end": v(-1063, 1879.27) * mm});
            skPoint(sketch, "E166.visualSharp", {"position": v(-1032.1, 1838.45) * mm});
            skArc(sketch, "E166.filletArc", {"start": v(-1037.6, 1835.28) * mm, "mid": v(-1034.64, 1839.14) * mm, "end": v(-1035.28, 1843.95) * mm});
            skPoint(sketch, "E167.visualSharp", {"position": v(-1076.1, 1813.05) * mm});
            skArc(sketch, "E167.filletArc", {"start": v(-1079.27, 1818.55) * mm, "mid": v(-1075.42, 1815.6) * mm, "end": v(-1070.6, 1816.23) * mm});
            skPoint(sketch, "E168.visualSharp", {"position": v(-1101.5, 1857.05) * mm});
            skArc(sketch, "E168.filletArc", {"start": v(-1096, 1860.22) * mm, "mid": v(-1098.96, 1856.37) * mm, "end": v(-1098.32, 1851.55) * mm});
            skLineSegment(sketch, "E169.0", {"start": v(-1059.25, 1875.94) * mm, "end": v(-1038.6, 1840.2) * mm});
            skLineSegment(sketch, "E169.1", {"start": v(-1059.25, 1875.94) * mm, "end": v(-1095, 1855.3) * mm});
            skLineSegment(sketch, "E169.2", {"start": v(-1095, 1855.3) * mm, "end": v(-1074.35, 1819.56) * mm});
            skLineSegment(sketch, "E169.3", {"start": v(-1038.6, 1840.2) * mm, "end": v(-1074.35, 1819.56) * mm});
            skSolve(sketch);
        }
        {
            var Q0;
            Q0=makeQuery(id+"F48.imprint","IMPRINT",FACE,{"disambiguationData":[TD([[makeQuery(id+"F48.imprint","IMPRINT",EDGE,{"derivedFrom":sQuery(id+"F48.wireOp",EDGE,"E164.bottom")}),1.0]])]});
            var Q1;
            Q1=sQuery(id+"F47.wireOp",EDGE,"E162");
            sweep(context, id + "F49", {"profiles" : qUnion([Q0]), "path" : qUnion([Q1])});
        }
        {
            var Q0;
            Q0=qCreatedBy(id+"F46.planeOp",FACE);
            var sketch = newSketch(context, id + "F50", { "sketchPlane" : qUnion([Q0])});
            skArc(sketch, "E170", {"start": v(-8585.2, 0) * mm, "mid": v(-7967.72, 1490.72) * mm, "end": v(-6477, 2108.2) * mm});
            skSolve(sketch);
        }
        {
            var Q0;
            Q0=sQuery(id+"F45.wireOp",VERTEX,"E155.end");
            var Q1;
            Q1=sQuery(id+"F50.wireOp",VERTEX,"E170.start");
            var Q2;
            Q2=sQuery(id+"F2.wireOp",VERTEX,"E55");
            cPlane(context, id + "F51", {"entities" : qUnion([Q0, Q1, Q2]), "cplaneType" : CPlaneType.THREE_POINT, "offset" : 25.4 * mm, "width" : 152.4 * mm, "height" : 152.4 * mm});
        }
        {
            var Q0;
            Q0=qCreatedBy(id+"F51.planeOp",FACE);
            var sketch = newSketch(context, id + "F52", { "sketchPlane" : qUnion([Q0])});
            skArc(sketch, "E171", {"start": v(-8585.2, 0) * mm, "mid": v(-7967.72, 1490.72) * mm, "end": v(-6477, 2108.2) * mm});
            skArc(sketch, "E172.0", {"start": v(-8559.8, 0) * mm, "mid": v(-7949.76, 1472.76) * mm, "end": v(-6477, 2082.8) * mm});
            skArc(sketch, "E173.0", {"start": v(-8610.6, 0) * mm, "mid": v(-7985.68, 1508.68) * mm, "end": v(-6477, 2133.6) * mm});
            skLineSegment(sketch, "E174", {"start": v(-6477, 2133.6) * mm, "end": v(-6432.7, 2133.6) * mm});
            skLineSegment(sketch, "E175", {"start": v(-6432.7, 2133.6) * mm, "end": v(-6432.7, 2082.8) * mm});
            skLineSegment(sketch, "E176", {"start": v(-6432.7, 2082.8) * mm, "end": v(-6477, 2082.8) * mm});
            skLineSegment(sketch, "E177", {"start": v(-8559.8, 0) * mm, "end": v(-8559.8, -33.94) * mm});
            skLineSegment(sketch, "E178", {"start": v(-8559.8, -33.94) * mm, "end": v(-8610.6, -33.94) * mm});
            skLineSegment(sketch, "E179", {"start": v(-8610.6, -33.94) * mm, "end": v(-8610.6, 0) * mm});
            skSolve(sketch);
        }
        {
            var Q0;
            Q0=qCreatedBy(id+"F44.planeOp",FACE);
            var sketch = newSketch(context, id + "F53", { "sketchPlane" : qUnion([Q0])});
            skLineSegment(sketch, "E180", {"start": v(0, 2108.2) * mm, "end": v(-1054.1, 1825.75) * mm});
            skLineSegment(sketch, "E181", {"start": v(-1054.1, 1825.75) * mm, "end": v(-1047.53, 1814.37) * mm});
            skLineSegment(sketch, "E182", {"start": v(-1047.53, 1814.37) * mm, "end": v(0, 2095.05) * mm});
            skLineSegment(sketch, "E183", {"start": v(0, 2095.05) * mm, "end": v(0, 2108.2) * mm});
            skLineSegment(sketch, "E184", {"start": v(-747.28, -200.23) * mm, "end": v(1032.17, 276.57) * mm});
            skPoint(sketch, "E185", {"position": v(-527.05, 1966.98) * mm});
            skSolve(sketch);
        }
        {
            var Q0;
            Q0=qCreatedBy(makeId("Front.planeOp"),FACE);
            var sketch = newSketch(context, id + "F54", { "sketchPlane" : qUnion([Q0])});
            skLineSegment(sketch, "E186", {"start": v(-3133.53, 1992.92) * mm, "end": v(-898.33, 1992.92) * mm, "construction": true});
            skLineSegment(sketch, "E187", {"start": v(-898.33, 1992.92) * mm, "end": v(-898.33, 4228.12) * mm, "construction": true});
            skArc(sketch, "E188", {"start": v(-3133.53, 1992.92) * mm, "mid": v(-2478.86, 3573.44) * mm, "end": v(-898.33, 4228.12) * mm});
            skArc(sketch, "E189.0", {"start": v(-3120.83, 1992.92) * mm, "mid": v(-2469.88, 3564.46) * mm, "end": v(-898.33, 4215.42) * mm});
            skLineSegment(sketch, "E190", {"start": v(-898.33, 4228.12) * mm, "end": v(-898.33, 4215.42) * mm});
            skLineSegment(sketch, "E191", {"start": v(-3133.53, 1992.92) * mm, "end": v(-3120.83, 1992.92) * mm});
            skSolve(sketch);
        }
        {
            var Q0;
            Q0=qSketchRegion(id+"F54",true);
            extrude(context, id + "F55", {"entities" : qUnion([Q0]), "depth" : 1270 * mm});
        }
        {
            var Q0;
            Q0=makeQuery(id+"F55.opExtrude","SWEPT_FACE",FACE,{"disambiguationData":[OSD([sQuery(id+"F54.wireOp",EDGE,"E190")])]});
            var sketch = newSketch(context, id + "F56", { "sketchPlane" : qUnion([Q0])});
            skLineSegment(sketch, "E192", {"start": v(-1233.92, 4228.12) * mm, "end": v(-635, 1992.92) * mm});
            skLineSegment(sketch, "E193", {"start": v(-635, 1992.92) * mm, "end": v(-36.08, 4228.12) * mm});
            skLineSegment(sketch, "E194", {"start": v(-36.08, 4228.12) * mm, "end": v(-1233.92, 4228.12) * mm});
            skLineSegment(sketch, "E195", {"start": v(-635, 4228.12) * mm, "end": v(-635, 1992.92) * mm, "construction": true});
            skSolve(sketch);
        }
        {
            var Q0;
            Q0=sQuery(id+"F56.wireOp",EDGE,"E195");
            cPlane(context, id + "F57", {"entities" : qUnion([Q0]), "cplaneType" : CPlaneType.LINE_ANGLE, "offset" : 25.4 * mm, "angle" : 90 * degree, "width" : 152.4 * mm, "height" : 152.4 * mm});
        }
        {
            var Q0;
            {var subQ0=sQuery(id+"F56.wireOp",EDGE,"E193");var subQ1=sQuery(id+"F56.wireOp",EDGE,"E192");var subQ2=makeQuery(id+"F56.imprint","INTERSECT",VERTEX,{"derivedFrom":[subQ1,subQ0]});Q0=makeQuery(id+"F56.imprint","IMPRINT",FACE,{"disambiguationData":[TD([[makeQuery(id+"F56.imprint","IMPRINT",EDGE,{"disambiguationData":[TD([[subQ2,1.0]])],"derivedFrom":subQ1}),1.0]])]});}
            var Q1;
            {var subQ0=sQuery(id+"F56.wireOp",EDGE,"E194");Q1=makeQuery(id+"F56.imprint","IMPRINT",FACE,{"disambiguationData":[TD([[makeQuery(id+"F56.imprint","IMPRINT",EDGE,{"derivedFrom":subQ0}),-1.0]])]});}
            extrude(context, id + "F58", {"entities" : qUnion([Q0, Q1]), "operationType" : NewBodyOperationType.INTERSECT, "endBound" : BoundingType.THROUGH_ALL, "oppositeDirection" : true, "depth" : 25.4 * mm});
        }
        {
            var Q0;
            Q0=sQuery(id+"F53.wireOp",VERTEX,"E185");
            var Q1;
            Q1=sQuery(id+"F52.wireOp",VERTEX,"E171.center");
            var Q2;
            Q2=sQuery(id+"F2.wireOp",VERTEX,"E55");
            cPlane(context, id + "F59", {"entities" : qUnion([Q0, Q1, Q2]), "cplaneType" : CPlaneType.THREE_POINT, "offset" : 25.4 * mm, "width" : 152.4 * mm, "height" : 152.4 * mm});
        }
        {
            var Q0;
            Q0=qCreatedBy(id+"F59.planeOp",FACE);
            var sketch = newSketch(context, id + "F60", { "sketchPlane" : qUnion([Q0])});
            skArc(sketch, "E196", {"start": v(-6477, 2036.36) * mm, "mid": v(-7764.8, 1577.45) * mm, "end": v(-8472.17, 407.55) * mm});
            skSolve(sketch);
        }
        {
            var Q0;
            Q0=makeQuery(id+"F53.imprint","IMPRINT",FACE,{"disambiguationData":[TD([[makeQuery(id+"F53.imprint","IMPRINT",EDGE,{"derivedFrom":sQuery(id+"F53.wireOp",EDGE,"E180")}),1.0]])]});
            var Q1;
            Q1=sQuery(id+"F60.wireOp",EDGE,"E196");
            sweep(context, id + "F61", {"profiles" : qUnion([Q0]), "path" : qUnion([Q1])});
        }
        {
            var Q0;
            Q0=qCreatedBy(id+"F59.planeOp",FACE);
            var sketch = newSketch(context, id + "F62", { "sketchPlane" : qUnion([Q0])});
            skEllipticalArc(sketch, "E197.0", {});
            const initialGuessF62  = {"E197.0": [-6.858, 0, 1, 0, 2.2352, 2.159037406921327, 1.5707963267948968, 3.141592653589793]};
            skSetInitialGuess(sketch, initialGuessF62);
            skSolve(sketch);
        }
        {
            var Q0;
            Q0=makeQuery(id+"F53.imprint","IMPRINT",FACE,{"disambiguationData":[TD([[makeQuery(id+"F53.imprint","IMPRINT",EDGE,{"derivedFrom":sQuery(id+"F53.wireOp",EDGE,"E180")}),1.0]])]});
            var Q1;
            Q1=sQuery(id+"F53.wireOp",EDGE,"E180");
            var Q2;
            Q2=sQuery(id+"F62.wireOp",EDGE,"E197.0");
            sweep(context, id + "F63", {"profiles" : qUnion([Q0]), "surfaceProfiles" : qUnion([Q1]), "path" : qUnion([Q2])});
        }
        {
            var Q0;
            Q0=qCreatedBy(id+"F44.planeOp",FACE);
            var sketch = newSketch(context, id + "F64", { "sketchPlane" : qUnion([Q0])});
            skLineSegment(sketch, "E198.0", {"start": v(0, 0) * mm, "end": v(-1054.1, 1825.75) * mm});
            skLineSegment(sketch, "E199.0", {"start": v(0, 0) * mm, "end": v(0, 2159) * mm});
            skLineSegment(sketch, "E200.0", {"start": v(0, 2108.2) * mm, "end": v(-1054.1, 1825.75) * mm});
            skSolve(sketch);
        }
        {
            var Q0;
            Q0=qSketchRegion(id+"F64",true);
            extrude(context, id + "F65", {"entities" : qUnion([Q0]), "operationType" : NewBodyOperationType.INTERSECT, "endBound" : BoundingType.THROUGH_ALL, "oppositeDirection" : true, "depth" : 25.4 * mm});
        }
        {
            var Q0;
            Q0=makeQuery(id+"F63.opSweep","SWEPT_BODY",BODY,{"disambiguationData":[OSD([sQuery(id+"F53.wireOp",EDGE,"E180"),sQuery(id+"F53.wireOp",EDGE,"E181"),sQuery(id+"F53.wireOp",EDGE,"E182"),sQuery(id+"F53.wireOp",EDGE,"E183"),sQuery(id+"F62.wireOp",EDGE,"E197.0")])]});
            var Q1;
            Q1=sQuery(id+"F2.wireOp",EDGE,"E41");
            circularPattern(context, id + "F66", {"entities" : qUnion([Q0]), "axis" : qUnion([Q1]), "angle" : 30 * degree, "instanceCount" : 12});
        }
        {
            var Q0;
            Q0=makeQuery(id+"F66.opPattern","COPY",VERTEX,{"derivedFrom":makeQuery(id+"F63.opSweep","CAP_VERTEX",VERTEX,{"disambiguationData":[OSD([sQuery(id+"F53.wireOp",EDGE,"E181"),sQuery(id+"F53.wireOp",EDGE,"E182"),sQuery(id+"F62.wireOp",EDGE,"E197.0")])],"isStart":true}),"instanceName":"6"});
            var Q1;
            Q1=qCreatedBy(makeId("Top.planeOp"),FACE);
            cPlane(context, id + "F67", {"entities" : qUnion([Q0, Q1]), "cplaneType" : CPlaneType.PLANE_POINT, "offset" : 25.4 * mm, "width" : 152.4 * mm, "height" : 152.4 * mm});
        }
    });
